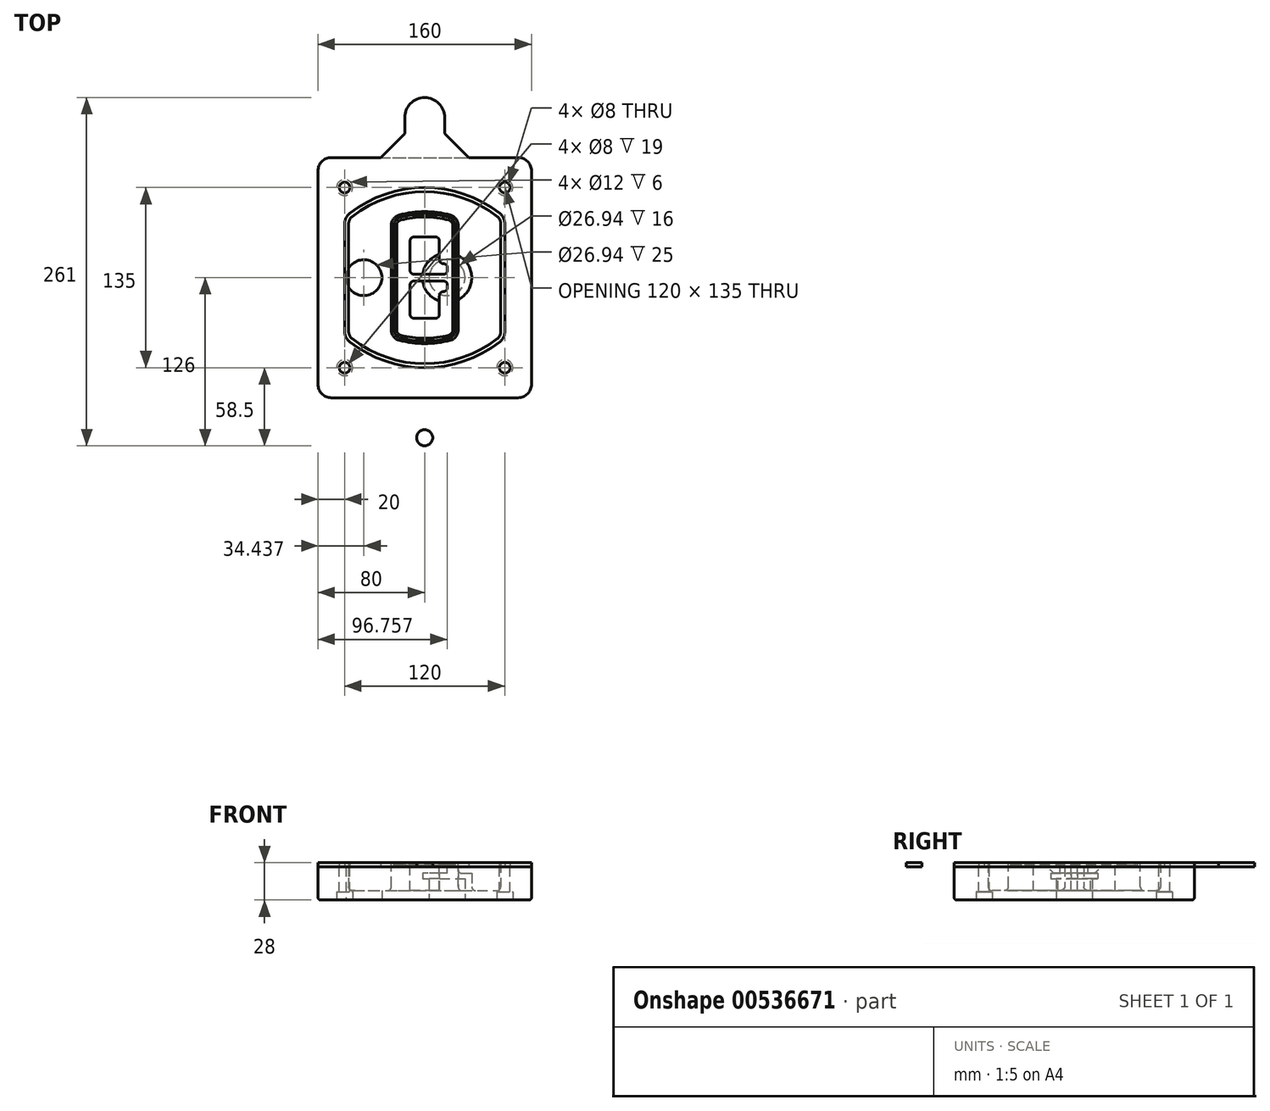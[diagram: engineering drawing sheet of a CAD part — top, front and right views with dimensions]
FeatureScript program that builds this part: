
annotation { "Feature Type Name" : "Feature", "Feature Type Description" : "" }
export const myFeature = defineFeature(function(context is Context, id is Id, definition is map)
    precondition{}
    {
        {
            var Q0;
            Q0=qCreatedBy(makeId("Top.planeOp"),FACE);
            var sketch = newSketch(context, id + "F0", { "sketchPlane" : qUnion([Q0])});
            skPoint(sketch, "E0.rect.middle", {"position": v(0, 0) * mm});
            skLineSegment(sketch, "E1.bottom", {"start": v(-70, -90) * mm, "end": v(70, -90) * mm});
            skLineSegment(sketch, "E1.top", {"start": v(-70, 90) * mm, "end": v(70, 90) * mm});
            skLineSegment(sketch, "E1.left", {"start": v(-80, -80) * mm, "end": v(-80, 80) * mm});
            skLineSegment(sketch, "E1.right", {"start": v(80, -80) * mm, "end": v(80, 80) * mm});
            skLineSegment(sketch, "E2", {"start": v(-80, 90) * mm, "end": v(80, -90) * mm, "construction": true});
            skLineSegment(sketch, "E3", {"start": v(80, 90) * mm, "end": v(-80, -90) * mm, "construction": true});
            skCircle(sketch, "E4", {"center": v(-60, 67.5) * mm, "radius": 4 * mm});
            skCircle(sketch, "E5", {"center": v(60, 67.5) * mm, "radius": 4 * mm});
            skCircle(sketch, "E6", {"center": v(60, -67.5) * mm, "radius": 4 * mm});
            skCircle(sketch, "E7", {"center": v(-60, -67.5) * mm, "radius": 4 * mm});
            skLineSegment(sketch, "E8", {"start": v(-60, 67.5) * mm, "end": v(60, 67.5) * mm, "construction": true});
            skLineSegment(sketch, "E9", {"start": v(60, 67.5) * mm, "end": v(60, -67.5) * mm, "construction": true});
            skLineSegment(sketch, "E10", {"start": v(60, -67.5) * mm, "end": v(-60, -67.5) * mm, "construction": true});
            skLineSegment(sketch, "E11", {"start": v(-60, -67.5) * mm, "end": v(-60, 67.5) * mm, "construction": true});
            skLineSegment(sketch, "E12", {"start": v(-60, 40.3) * mm, "end": v(-60, -40.3) * mm});
            skLineSegment(sketch, "E13", {"start": v(60, 40.3) * mm, "end": v(60, -40.3) * mm});
            skArc(sketch, "E14", {"start": v(56.15, 48.18) * mm, "mid": v(0, 67.5) * mm, "end": v(-56.15, 48.18) * mm});
            skArc(sketch, "E15", {"start": v(-56.15, -48.18) * mm, "mid": v(0, -67.5) * mm, "end": v(56.15, -48.18) * mm});
            skLineSegment(sketch, "E16", {"start": v(-60, 0) * mm, "end": v(60, 0) * mm, "construction": true});
            skPoint(sketch, "E17.visualSharp", {"position": v(-60, -45) * mm});
            skArc(sketch, "E17.filletArc", {"start": v(-60, -40.3) * mm, "mid": v(-58.99, -44.68) * mm, "end": v(-56.15, -48.18) * mm});
            skPoint(sketch, "E18.visualSharp", {"position": v(-60, 45) * mm});
            skArc(sketch, "E18.filletArc", {"start": v(-56.15, 48.18) * mm, "mid": v(-58.99, 44.68) * mm, "end": v(-60, 40.3) * mm});
            skPoint(sketch, "E19.visualSharp", {"position": v(60, 45) * mm});
            skArc(sketch, "E19.filletArc", {"start": v(60, 40.3) * mm, "mid": v(58.99, 44.68) * mm, "end": v(56.15, 48.18) * mm});
            skPoint(sketch, "E20.visualSharp", {"position": v(60, -45) * mm});
            skArc(sketch, "E20.filletArc", {"start": v(56.15, -48.18) * mm, "mid": v(58.99, -44.68) * mm, "end": v(60, -40.3) * mm});
            skPoint(sketch, "E21.visualSharp", {"position": v(-80, 90) * mm});
            skArc(sketch, "E21.filletArc", {"start": v(-70, 90) * mm, "mid": v(-77.07, 87.07) * mm, "end": v(-80, 80) * mm});
            skPoint(sketch, "E22.visualSharp", {"position": v(80, 90) * mm});
            skArc(sketch, "E22.filletArc", {"start": v(80, 80) * mm, "mid": v(77.07, 87.07) * mm, "end": v(70, 90) * mm});
            skPoint(sketch, "E23.visualSharp", {"position": v(80, -90) * mm});
            skArc(sketch, "E23.filletArc", {"start": v(70, -90) * mm, "mid": v(77.07, -87.07) * mm, "end": v(80, -80) * mm});
            skPoint(sketch, "E24.visualSharp", {"position": v(-80, -90) * mm});
            skArc(sketch, "E24.filletArc", {"start": v(-80, -80) * mm, "mid": v(-77.07, -87.07) * mm, "end": v(-70, -90) * mm});
            skArc(sketch, "E25.0", {"start": v(57, 40.3) * mm, "mid": v(56.3, 43.36) * mm, "end": v(54.3, 45.81) * mm});
            skLineSegment(sketch, "E25.1", {"start": v(57, 40.3) * mm, "end": v(57, -40.3) * mm});
            skArc(sketch, "E25.2", {"start": v(54.3, -45.81) * mm, "mid": v(56.3, -43.36) * mm, "end": v(57, -40.3) * mm});
            skArc(sketch, "E25.3", {"start": v(-54.3, -45.81) * mm, "mid": v(0, -64.5) * mm, "end": v(54.3, -45.81) * mm});
            skArc(sketch, "E25.4", {"start": v(-57, -40.3) * mm, "mid": v(-56.3, -43.36) * mm, "end": v(-54.3, -45.81) * mm});
            skArc(sketch, "E25.5", {"start": v(54.3, 45.81) * mm, "mid": v(0, 64.5) * mm, "end": v(-54.3, 45.81) * mm});
            skLineSegment(sketch, "E25.6", {"start": v(-57, 40.3) * mm, "end": v(-57, -40.3) * mm});
            skArc(sketch, "E25.7", {"start": v(-54.3, 45.81) * mm, "mid": v(-56.3, 43.36) * mm, "end": v(-57, 40.3) * mm});
            skArc(sketch, "E26.0", {"start": v(-58.62, 51.33) * mm, "mid": v(-62.58, 46.43) * mm, "end": v(-64, 40.3) * mm});
            skArc(sketch, "E26.1", {"start": v(58.62, 51.33) * mm, "mid": v(0, 71.5) * mm, "end": v(-58.62, 51.33) * mm});
            skArc(sketch, "E26.2", {"start": v(64, 40.3) * mm, "mid": v(62.58, 46.43) * mm, "end": v(58.62, 51.33) * mm});
            skLineSegment(sketch, "E26.3", {"start": v(64, 40.3) * mm, "end": v(64, -40.3) * mm});
            skArc(sketch, "E26.4", {"start": v(58.62, -51.33) * mm, "mid": v(62.58, -46.43) * mm, "end": v(64, -40.3) * mm});
            skLineSegment(sketch, "E26.5", {"start": v(-64, 40.3) * mm, "end": v(-64, -40.3) * mm});
            skArc(sketch, "E26.6", {"start": v(-58.62, -51.33) * mm, "mid": v(0, -71.5) * mm, "end": v(58.62, -51.33) * mm});
            skArc(sketch, "E26.7", {"start": v(-64, -40.3) * mm, "mid": v(-62.58, -46.43) * mm, "end": v(-58.62, -51.33) * mm});
            skSolve(sketch);
        }
        {
            var Q0;
            Q0=makeQuery(id+"F0.imprint","IMPRINT",FACE,{"disambiguationData":[TD([[makeQuery(id+"F0.imprint","IMPRINT",EDGE,{"derivedFrom":sQuery(id+"F0.wireOp",EDGE,"E1.bottom")}),1.0]])]});
            var Q1;
            Q1=makeQuery(id+"F0.imprint","IMPRINT",FACE,{"disambiguationData":[TD([[makeQuery(id+"F0.imprint","IMPRINT",EDGE,{"derivedFrom":sQuery(id+"F0.wireOp",EDGE,"E12")}),1.0]])]});
            var Q2;
            Q2=makeQuery(id+"F0.imprint","IMPRINT",FACE,{"disambiguationData":[TD([[makeQuery(id+"F0.imprint","IMPRINT",EDGE,{"derivedFrom":sQuery(id+"F0.wireOp",EDGE,"E25.0")}),1.0]])]});
            var Q3;
            Q3=makeQuery(id+"F0.imprint","IMPRINT",FACE,{"disambiguationData":[TD([[makeQuery(id+"F0.imprint","IMPRINT",EDGE,{"derivedFrom":sQuery(id+"F0.wireOp",EDGE,"E12")}),-1.0]])]});
            extrude(context, id + "F1", {"entities" : qUnion([Q0, Q1, Q2, Q3]), "oppositeDirection" : true, "depth" : 25 * mm});
        }
        {
            var Q0;
            Q0=makeQuery(id+"F0.imprint","IMPRINT",FACE,{"disambiguationData":[TD([[makeQuery(id+"F0.imprint","IMPRINT",EDGE,{"derivedFrom":sQuery(id+"F0.wireOp",EDGE,"E12")}),1.0]])]});
            extrude(context, id + "F2", {"entities" : qUnion([Q0]), "operationType" : NewBodyOperationType.ADD, "depth" : 3 * mm});
        }
        {
            var Q0;
            Q0=makeQuery(id+"F0.imprint","IMPRINT",FACE,{"disambiguationData":[TD([[makeQuery(id+"F0.imprint","IMPRINT",EDGE,{"derivedFrom":sQuery(id+"F0.wireOp",EDGE,"E25.0")}),1.0]])]});
            extrude(context, id + "F3", {"entities" : qUnion([Q0]), "operationType" : NewBodyOperationType.REMOVE, "oppositeDirection" : true, "depth" : 18 * mm});
        }
        {
            var Q0;
            Q0=makeQuery(id+"F2.opExtrude","CAP_FACE",FACE,{"disambiguationData":[OSD([sQuery(id+"F0.wireOp",EDGE,"E12"),sQuery(id+"F0.wireOp",EDGE,"E13"),sQuery(id+"F0.wireOp",EDGE,"E14"),sQuery(id+"F0.wireOp",EDGE,"E15"),sQuery(id+"F0.wireOp",EDGE,"E17.filletArc"),sQuery(id+"F0.wireOp",EDGE,"E18.filletArc"),sQuery(id+"F0.wireOp",EDGE,"E19.filletArc"),sQuery(id+"F0.wireOp",EDGE,"E20.filletArc"),sQuery(id+"F0.wireOp",EDGE,"E25.0"),sQuery(id+"F0.wireOp",EDGE,"E25.1"),sQuery(id+"F0.wireOp",EDGE,"E25.2"),sQuery(id+"F0.wireOp",EDGE,"E25.3"),sQuery(id+"F0.wireOp",EDGE,"E25.4"),sQuery(id+"F0.wireOp",EDGE,"E25.5"),sQuery(id+"F0.wireOp",EDGE,"E25.6"),sQuery(id+"F0.wireOp",EDGE,"E25.7")])],"isStart":false});
            var sketch = newSketch(context, id + "F4", { "sketchPlane" : qUnion([Q0])});
            skArc(sketch, "E27.0", {"start": v(-19.08, -46.97) * mm, "mid": v(0, -49.5) * mm, "end": v(19.08, -46.97) * mm});
            skArc(sketch, "E28.0", {"start": v(19.08, 46.97) * mm, "mid": v(0, 49.5) * mm, "end": v(-19.08, 46.97) * mm});
            skLineSegment(sketch, "E29", {"start": v(-25, 39.25) * mm, "end": v(-25, -39.25) * mm});
            skLineSegment(sketch, "E30", {"start": v(25, 39.25) * mm, "end": v(25, -39.25) * mm});
            skLineSegment(sketch, "E31", {"start": v(-25, 45.1) * mm, "end": v(25, 45.1) * mm, "construction": true});
            skLineSegment(sketch, "E32", {"start": v(-25, -45.1) * mm, "end": v(25, -45.1) * mm, "construction": true});
            skPoint(sketch, "E33.visualSharp", {"position": v(-25, 45.1) * mm});
            skArc(sketch, "E33.filletArc", {"start": v(-19.08, 46.97) * mm, "mid": v(-23.35, 44.11) * mm, "end": v(-25, 39.25) * mm});
            skPoint(sketch, "E34.visualSharp", {"position": v(25, 45.1) * mm});
            skArc(sketch, "E34.filletArc", {"start": v(25, 39.25) * mm, "mid": v(23.35, 44.11) * mm, "end": v(19.08, 46.97) * mm});
            skPoint(sketch, "E35.visualSharp", {"position": v(25, -45.1) * mm});
            skArc(sketch, "E35.filletArc", {"start": v(19.08, -46.97) * mm, "mid": v(23.35, -44.11) * mm, "end": v(25, -39.25) * mm});
            skPoint(sketch, "E36.visualSharp", {"position": v(-25, -45.1) * mm});
            skArc(sketch, "E36.filletArc", {"start": v(-25, -39.25) * mm, "mid": v(-23.35, -44.11) * mm, "end": v(-19.08, -46.97) * mm});
            skArc(sketch, "E37.0", {"start": v(54.3, 45.81) * mm, "mid": v(0, 64.5) * mm, "end": v(-54.3, 45.81) * mm});
            skArc(sketch, "E37.1", {"start": v(-54.3, 45.81) * mm, "mid": v(-56.3, 43.36) * mm, "end": v(-57, 40.3) * mm});
            skLineSegment(sketch, "E37.2", {"start": v(-57, 40.3) * mm, "end": v(-57, -40.3) * mm});
            skArc(sketch, "E37.3", {"start": v(-57, -40.3) * mm, "mid": v(-56.3, -43.36) * mm, "end": v(-54.3, -45.81) * mm});
            skArc(sketch, "E37.4", {"start": v(-54.3, -45.81) * mm, "mid": v(0, -64.5) * mm, "end": v(54.3, -45.81) * mm});
            skArc(sketch, "E37.5", {"start": v(54.3, -45.81) * mm, "mid": v(56.3, -43.36) * mm, "end": v(57, -40.3) * mm});
            skLineSegment(sketch, "E37.6", {"start": v(57, 40.3) * mm, "end": v(57, -40.3) * mm});
            skArc(sketch, "E37.7", {"start": v(57, 40.3) * mm, "mid": v(56.3, 43.36) * mm, "end": v(54.3, 45.81) * mm});
            skLineSegment(sketch, "E38.0", {"start": v(23, 39.25) * mm, "end": v(23, -39.25) * mm});
            skArc(sketch, "E38.1", {"start": v(18.56, -45.04) * mm, "mid": v(21.76, -42.9) * mm, "end": v(23, -39.25) * mm});
            skArc(sketch, "E38.2", {"start": v(-18.56, -45.04) * mm, "mid": v(0, -47.5) * mm, "end": v(18.56, -45.04) * mm});
            skArc(sketch, "E38.3", {"start": v(-23, -39.25) * mm, "mid": v(-21.76, -42.9) * mm, "end": v(-18.56, -45.04) * mm});
            skLineSegment(sketch, "E38.4", {"start": v(-23, 39.25) * mm, "end": v(-23, -39.25) * mm});
            skArc(sketch, "E38.5", {"start": v(23, 39.25) * mm, "mid": v(21.76, 42.9) * mm, "end": v(18.56, 45.04) * mm});
            skArc(sketch, "E38.6", {"start": v(-18.56, 45.04) * mm, "mid": v(-21.76, 42.9) * mm, "end": v(-23, 39.25) * mm});
            skArc(sketch, "E38.7", {"start": v(18.56, 45.04) * mm, "mid": v(0, 47.5) * mm, "end": v(-18.56, 45.04) * mm});
            skArc(sketch, "E39.0", {"start": v(21, 39.25) * mm, "mid": v(20.18, 41.68) * mm, "end": v(18.04, 43.1) * mm});
            skLineSegment(sketch, "E39.1", {"start": v(21, 39.25) * mm, "end": v(21, -39.25) * mm});
            skArc(sketch, "E39.2", {"start": v(18.04, -43.1) * mm, "mid": v(20.18, -41.68) * mm, "end": v(21, -39.25) * mm});
            skArc(sketch, "E39.3", {"start": v(-18.04, -43.1) * mm, "mid": v(0, -45.5) * mm, "end": v(18.04, -43.1) * mm});
            skArc(sketch, "E39.4", {"start": v(-21, -39.25) * mm, "mid": v(-20.18, -41.68) * mm, "end": v(-18.04, -43.1) * mm});
            skArc(sketch, "E39.5", {"start": v(18.04, 43.1) * mm, "mid": v(0, 45.5) * mm, "end": v(-18.04, 43.1) * mm});
            skLineSegment(sketch, "E39.6", {"start": v(-21, 39.25) * mm, "end": v(-21, -39.25) * mm});
            skArc(sketch, "E39.7", {"start": v(-18.04, 43.1) * mm, "mid": v(-20.18, 41.68) * mm, "end": v(-21, 39.25) * mm});
            skLineSegment(sketch, "E40", {"start": v(-25, 0) * mm, "end": v(25, 0) * mm, "construction": true});
            skLineSegment(sketch, "E41", {"start": v(-11, 5.5) * mm, "end": v(-11, 27.5) * mm});
            skLineSegment(sketch, "E42", {"start": v(-8, 30.5) * mm, "end": v(8, 30.5) * mm});
            skLineSegment(sketch, "E43", {"start": v(11, 27.5) * mm, "end": v(11, 13.5) * mm});
            skLineSegment(sketch, "E44", {"start": v(14, 10.5) * mm, "end": v(14, 10.5) * mm});
            skLineSegment(sketch, "E45", {"start": v(17, 7.5) * mm, "end": v(17, 5.5) * mm});
            skLineSegment(sketch, "E46", {"start": v(14, 2.5) * mm, "end": v(-8, 2.5) * mm});
            skPoint(sketch, "E47.visualSharp", {"position": v(-11, 30.5) * mm});
            skArc(sketch, "E47.filletArc", {"start": v(-8, 30.5) * mm, "mid": v(-10.12, 29.62) * mm, "end": v(-11, 27.5) * mm});
            skPoint(sketch, "E48.visualSharp", {"position": v(11, 30.5) * mm});
            skArc(sketch, "E48.filletArc", {"start": v(11, 27.5) * mm, "mid": v(10.12, 29.62) * mm, "end": v(8, 30.5) * mm});
            skPoint(sketch, "E49.visualSharp", {"position": v(11, 10.5) * mm});
            skArc(sketch, "E49.filletArc", {"start": v(11, 13.5) * mm, "mid": v(11.88, 11.38) * mm, "end": v(14, 10.5) * mm});
            skPoint(sketch, "E50.visualSharp", {"position": v(17, 10.5) * mm});
            skArc(sketch, "E50.filletArc", {"start": v(17, 7.5) * mm, "mid": v(16.12, 9.62) * mm, "end": v(14, 10.5) * mm});
            skPoint(sketch, "E51.visualSharp", {"position": v(17, 2.5) * mm});
            skArc(sketch, "E51.filletArc", {"start": v(14, 2.5) * mm, "mid": v(16.12, 3.38) * mm, "end": v(17, 5.5) * mm});
            skPoint(sketch, "E52.visualSharp", {"position": v(-11, 2.5) * mm});
            skArc(sketch, "E52.filletArc", {"start": v(-11, 5.5) * mm, "mid": v(-10.12, 3.38) * mm, "end": v(-8, 2.5) * mm});
            skLineSegment(sketch, "E53.0.MirrorCS", {"start": v(14, -2.5) * mm, "end": v(-8, -2.5) * mm});
            skArc(sketch, "E54.0.MirrorCS", {"start": v(-11, -5.5) * mm, "mid": v(-10.12, -3.38) * mm, "end": v(-8, -2.5) * mm});
            skLineSegment(sketch, "E55.0.MirrorCS", {"start": v(-11, -5.5) * mm, "end": v(-11, -27.5) * mm});
            skArc(sketch, "E56.0.MirrorCS", {"start": v(-8, -30.5) * mm, "mid": v(-10.12, -29.62) * mm, "end": v(-11, -27.5) * mm});
            skLineSegment(sketch, "E57.0.MirrorCS", {"start": v(-8, -30.5) * mm, "end": v(8, -30.5) * mm});
            skArc(sketch, "E58.0.MirrorCS", {"start": v(11, -27.5) * mm, "mid": v(10.12, -29.62) * mm, "end": v(8, -30.5) * mm});
            skLineSegment(sketch, "E59.0.MirrorCS", {"start": v(11, -27.5) * mm, "end": v(11, -13.5) * mm});
            skArc(sketch, "E60.0.MirrorCS", {"start": v(11, -13.5) * mm, "mid": v(11.88, -11.38) * mm, "end": v(14, -10.5) * mm});
            skArc(sketch, "E61.0.MirrorCS", {"start": v(17, -7.5) * mm, "mid": v(16.12, -9.62) * mm, "end": v(14, -10.5) * mm});
            skLineSegment(sketch, "E62.0.MirrorCS", {"start": v(17, -7.5) * mm, "end": v(17, -5.5) * mm});
            skArc(sketch, "E63.0.MirrorCS", {"start": v(14, -2.5) * mm, "mid": v(16.12, -3.38) * mm, "end": v(17, -5.5) * mm});
            skSolve(sketch);
        }
        {
            var Q0;
            Q0=makeQuery(id+"F4.imprint","IMPRINT",FACE,{"disambiguationData":[TD([[makeQuery(id+"F4.imprint","IMPRINT",EDGE,{"derivedFrom":sQuery(id+"F4.wireOp",EDGE,"E27.0")}),1.0]])]});
            var Q1;
            Q1=makeQuery(id+"F4.imprint","IMPRINT",FACE,{"disambiguationData":[TD([[makeQuery(id+"F4.imprint","IMPRINT",EDGE,{"derivedFrom":sQuery(id+"F4.wireOp",EDGE,"E38.0")}),-1.0]])]});
            var Q2;
            Q2=makeQuery(id+"F4.imprint","IMPRINT",FACE,{"disambiguationData":[TD([[makeQuery(id+"F4.imprint","IMPRINT",EDGE,{"derivedFrom":sQuery(id+"F4.wireOp",EDGE,"E39.0")}),1.0]])]});
            extrude(context, id + "F5", {"entities" : qUnion([Q0, Q1, Q2]), "operationType" : NewBodyOperationType.ADD, "endBound" : BoundingType.UP_TO_NEXT, "oppositeDirection" : true, "depth" : 25 * mm});
        }
        {
            var Q0;
            Q0=makeQuery(id+"F4.imprint","IMPRINT",FACE,{"disambiguationData":[TD([[makeQuery(id+"F4.imprint","IMPRINT",EDGE,{"derivedFrom":sQuery(id+"F4.wireOp",EDGE,"E38.0")}),-1.0]])]});
            extrude(context, id + "F6", {"entities" : qUnion([Q0]), "operationType" : NewBodyOperationType.REMOVE, "oppositeDirection" : true, "depth" : 2 * mm});
        }
        {
            var Q0;
            Q0=makeQuery(id+"F1.opExtrude","CAP_FACE",FACE,{"disambiguationData":[OSD([sQuery(id+"F0.wireOp",EDGE,"E1.bottom"),sQuery(id+"F0.wireOp",EDGE,"E1.top"),sQuery(id+"F0.wireOp",EDGE,"E1.left"),sQuery(id+"F0.wireOp",EDGE,"E1.right"),sQuery(id+"F0.wireOp",EDGE,"E4"),sQuery(id+"F0.wireOp",EDGE,"E5"),sQuery(id+"F0.wireOp",EDGE,"E6"),sQuery(id+"F0.wireOp",EDGE,"E7"),sQuery(id+"F0.wireOp",EDGE,"E21.filletArc"),sQuery(id+"F0.wireOp",EDGE,"E22.filletArc"),sQuery(id+"F0.wireOp",EDGE,"E23.filletArc"),sQuery(id+"F0.wireOp",EDGE,"E24.filletArc")])],"isStart":false});
            var sketch = newSketch(context, id + "F7", { "sketchPlane" : qUnion([Q0])});
            skCircle(sketch, "E64", {"center": v(16.76, 0) * mm, "radius": 13.47 * mm});
            skCircle(sketch, "E65", {"center": v(-45.56, 0) * mm, "radius": 13.47 * mm});
            skLineSegment(sketch, "E66", {"start": v(80, 0) * mm, "end": v(-80, 0) * mm});
            skCircle(sketch, "E67", {"center": v(16.76, 0) * mm, "radius": 18.47 * mm});
            skCircle(sketch, "E68", {"center": v(60, -67.5) * mm, "radius": 6 * mm});
            skCircle(sketch, "E69", {"center": v(-60, -67.5) * mm, "radius": 6 * mm});
            skCircle(sketch, "E70", {"center": v(-60, 67.5) * mm, "radius": 6 * mm});
            skCircle(sketch, "E71", {"center": v(60, 67.5) * mm, "radius": 6 * mm});
            skSolve(sketch);
        }
        {
            var Q0;
            {var subQ1=sQuery(id+"F7.wireOp",EDGE,"E66");var subQ4=sQuery(id+"F7.wireOp",EDGE,"E64");var subQ6=makeQuery(id+"F7.imprint","INTERSECT",VERTEX,{"disambiguationData":[OD(0.0)],"derivedFrom":[subQ4,subQ1]});Q0=makeQuery(id+"F7.imprint","IMPRINT",FACE,{"disambiguationData":[TD([[makeQuery(id+"F7.imprint","IMPRINT",EDGE,{"disambiguationData":[TD([[subQ6,-1.0]])],"derivedFrom":subQ4}),-1.0]])]});}
            var Q1;
            {var subQ0=sQuery(id+"F7.wireOp",EDGE,"E66");var subQ1=sQuery(id+"F7.wireOp",EDGE,"E64");var subQ3=makeQuery(id+"F7.imprint","INTERSECT",VERTEX,{"disambiguationData":[OD(0.0)],"derivedFrom":[subQ1,subQ0]});Q1=makeQuery(id+"F7.imprint","IMPRINT",FACE,{"disambiguationData":[TD([[makeQuery(id+"F7.imprint","IMPRINT",EDGE,{"disambiguationData":[TD([[subQ3,-1.0]])],"derivedFrom":subQ1}),1.0]])]});}
            var Q2;
            {var subQ0=sQuery(id+"F7.wireOp",EDGE,"E66");var subQ1=sQuery(id+"F7.wireOp",EDGE,"E64");var subQ3=makeQuery(id+"F7.imprint","INTERSECT",VERTEX,{"disambiguationData":[OD(0.0)],"derivedFrom":[subQ1,subQ0]});Q2=makeQuery(id+"F7.imprint","IMPRINT",FACE,{"disambiguationData":[TD([[makeQuery(id+"F7.imprint","IMPRINT",EDGE,{"disambiguationData":[TD([[subQ3,1.0]])],"derivedFrom":subQ1}),1.0]])]});}
            var Q3;
            {var subQ1=sQuery(id+"F7.wireOp",EDGE,"E66");var subQ4=sQuery(id+"F7.wireOp",EDGE,"E64");var subQ6=makeQuery(id+"F7.imprint","INTERSECT",VERTEX,{"disambiguationData":[OD(0.0)],"derivedFrom":[subQ4,subQ1]});Q3=makeQuery(id+"F7.imprint","IMPRINT",FACE,{"disambiguationData":[TD([[makeQuery(id+"F7.imprint","IMPRINT",EDGE,{"disambiguationData":[TD([[subQ6,1.0]])],"derivedFrom":subQ4}),-1.0]])]});}
            extrude(context, id + "F8", {"entities" : qUnion([Q0, Q1, Q2, Q3]), "operationType" : NewBodyOperationType.ADD, "oppositeDirection" : true, "depth" : 20 * mm});
        }
        {
            var Q0;
            {var subQ0=sQuery(id+"F7.wireOp",EDGE,"E66");var subQ1=sQuery(id+"F7.wireOp",EDGE,"E64");var subQ3=makeQuery(id+"F7.imprint","INTERSECT",VERTEX,{"disambiguationData":[OD(0.0)],"derivedFrom":[subQ1,subQ0]});Q0=makeQuery(id+"F7.imprint","IMPRINT",FACE,{"disambiguationData":[TD([[makeQuery(id+"F7.imprint","IMPRINT",EDGE,{"disambiguationData":[TD([[subQ3,-1.0]])],"derivedFrom":subQ1}),1.0]])]});}
            var Q1;
            {var subQ0=sQuery(id+"F7.wireOp",EDGE,"E66");var subQ1=sQuery(id+"F7.wireOp",EDGE,"E64");var subQ3=makeQuery(id+"F7.imprint","INTERSECT",VERTEX,{"disambiguationData":[OD(0.0)],"derivedFrom":[subQ1,subQ0]});Q1=makeQuery(id+"F7.imprint","IMPRINT",FACE,{"disambiguationData":[TD([[makeQuery(id+"F7.imprint","IMPRINT",EDGE,{"disambiguationData":[TD([[subQ3,1.0]])],"derivedFrom":subQ1}),1.0]])]});}
            extrude(context, id + "F9", {"entities" : qUnion([Q0, Q1]), "operationType" : NewBodyOperationType.REMOVE, "oppositeDirection" : true, "depth" : 16 * mm});
        }
        {
            var Q0;
            {var subQ0=sQuery(id+"F7.wireOp",EDGE,"E66");var subQ1=sQuery(id+"F7.wireOp",EDGE,"E65");var subQ3=makeQuery(id+"F7.imprint","INTERSECT",VERTEX,{"disambiguationData":[OD(0.0)],"derivedFrom":[subQ1,subQ0]});Q0=makeQuery(id+"F7.imprint","IMPRINT",FACE,{"disambiguationData":[TD([[makeQuery(id+"F7.imprint","IMPRINT",EDGE,{"disambiguationData":[TD([[subQ3,-1.0]])],"derivedFrom":subQ1}),1.0]])]});}
            var Q1;
            {var subQ0=sQuery(id+"F7.wireOp",EDGE,"E66");var subQ1=sQuery(id+"F7.wireOp",EDGE,"E65");var subQ3=makeQuery(id+"F7.imprint","INTERSECT",VERTEX,{"disambiguationData":[OD(0.0)],"derivedFrom":[subQ1,subQ0]});Q1=makeQuery(id+"F7.imprint","IMPRINT",FACE,{"disambiguationData":[TD([[makeQuery(id+"F7.imprint","IMPRINT",EDGE,{"disambiguationData":[TD([[subQ3,1.0]])],"derivedFrom":subQ1}),1.0]])]});}
            extrude(context, id + "F10", {"entities" : qUnion([Q0, Q1]), "operationType" : NewBodyOperationType.REMOVE, "oppositeDirection" : true, "depth" : 25 * mm});
        }
        {
            var Q0;
            Q0=makeQuery(id+"F7.imprint","IMPRINT",FACE,{"disambiguationData":[TD([[makeQuery(id+"F7.imprint","IMPRINT",EDGE,{"derivedFrom":sQuery(id+"F7.wireOp",EDGE,"E68")}),1.0]])]});
            var Q1;
            Q1=makeQuery(id+"F7.imprint","IMPRINT",FACE,{"disambiguationData":[TD([[makeQuery(id+"F7.imprint","IMPRINT",EDGE,{"derivedFrom":makeQuery(id+"F1.opExtrude","CAP_EDGE",EDGE,{"disambiguationData":[OSD([sQuery(id+"F0.wireOp",EDGE,"E5")])],"isStart":false})}),-1.0]])]});
            var Q2;
            Q2=makeQuery(id+"F7.imprint","IMPRINT",FACE,{"disambiguationData":[TD([[makeQuery(id+"F7.imprint","IMPRINT",EDGE,{"derivedFrom":sQuery(id+"F7.wireOp",EDGE,"E69")}),1.0]])]});
            var Q3;
            Q3=makeQuery(id+"F7.imprint","IMPRINT",FACE,{"disambiguationData":[TD([[makeQuery(id+"F7.imprint","IMPRINT",EDGE,{"derivedFrom":makeQuery(id+"F1.opExtrude","CAP_EDGE",EDGE,{"disambiguationData":[OSD([sQuery(id+"F0.wireOp",EDGE,"E4")])],"isStart":false})}),-1.0]])]});
            var Q4;
            Q4=makeQuery(id+"F7.imprint","IMPRINT",FACE,{"disambiguationData":[TD([[makeQuery(id+"F7.imprint","IMPRINT",EDGE,{"derivedFrom":sQuery(id+"F7.wireOp",EDGE,"E70")}),1.0]])]});
            var Q5;
            Q5=makeQuery(id+"F7.imprint","IMPRINT",FACE,{"disambiguationData":[TD([[makeQuery(id+"F7.imprint","IMPRINT",EDGE,{"derivedFrom":makeQuery(id+"F1.opExtrude","CAP_EDGE",EDGE,{"disambiguationData":[OSD([sQuery(id+"F0.wireOp",EDGE,"E7")])],"isStart":false})}),-1.0]])]});
            var Q6;
            Q6=makeQuery(id+"F7.imprint","IMPRINT",FACE,{"disambiguationData":[TD([[makeQuery(id+"F7.imprint","IMPRINT",EDGE,{"derivedFrom":sQuery(id+"F7.wireOp",EDGE,"E71")}),1.0]])]});
            var Q7;
            Q7=makeQuery(id+"F7.imprint","IMPRINT",FACE,{"disambiguationData":[TD([[makeQuery(id+"F7.imprint","IMPRINT",EDGE,{"derivedFrom":makeQuery(id+"F1.opExtrude","CAP_EDGE",EDGE,{"disambiguationData":[OSD([sQuery(id+"F0.wireOp",EDGE,"E6")])],"isStart":false})}),-1.0]])]});
            extrude(context, id + "F11", {"entities" : qUnion([Q0, Q1, Q2, Q3, Q4, Q5, Q6, Q7]), "operationType" : NewBodyOperationType.REMOVE, "oppositeDirection" : true, "depth" : 6 * mm});
        }
        {
            var Q0;
            Q0=makeQuery(id+"F9.boolean.opBoolean","COPY",FACE,{"derivedFrom":makeQuery(id+"F9.opExtrude","CAP_FACE",FACE,{"disambiguationData":[OSD([sQuery(id+"F7.wireOp",EDGE,"E64")])],"isStart":false})});
            var sketch = newSketch(context, id + "F12", { "sketchPlane" : qUnion([Q0])});
            skArc(sketch, "E72.0", {"start": v(11, 17.55) * mm, "mid": v(2.57, 11.82) * mm, "end": v(-1.54, 2.5) * mm});
            skArc(sketch, "E72.1", {"start": v(-1.54, -2.5) * mm, "mid": v(2.57, -11.82) * mm, "end": v(11, -17.55) * mm});
            skLineSegment(sketch, "E73", {"start": v(-1.54, -2.5) * mm, "end": v(14, -2.5) * mm});
            skLineSegment(sketch, "E74.0", {"start": v(14, 2.5) * mm, "end": v(-1.54, 2.5) * mm});
            skArc(sketch, "E74.1", {"start": v(14, 2.5) * mm, "mid": v(16.12, 3.38) * mm, "end": v(17, 5.5) * mm});
            skLineSegment(sketch, "E74.2", {"start": v(17, 7.5) * mm, "end": v(17, 5.5) * mm});
            skArc(sketch, "E74.3", {"start": v(17, 7.5) * mm, "mid": v(16.12, 9.62) * mm, "end": v(14, 10.5) * mm});
            skArc(sketch, "E74.4", {"start": v(11, 13.5) * mm, "mid": v(11.88, 11.38) * mm, "end": v(14, 10.5) * mm});
            skLineSegment(sketch, "E74.5", {"start": v(11, 17.55) * mm, "end": v(11, 13.5) * mm});
            skLineSegment(sketch, "E74.7", {"start": v(14, -2.5) * mm, "end": v(-1.54, -2.5) * mm});
            skArc(sketch, "E74.8", {"start": v(14, -2.5) * mm, "mid": v(16.12, -3.38) * mm, "end": v(17, -5.5) * mm});
            skLineSegment(sketch, "E74.9", {"start": v(17, -7.5) * mm, "end": v(17, -5.5) * mm});
            skArc(sketch, "E74.10", {"start": v(17, -7.5) * mm, "mid": v(16.12, -9.62) * mm, "end": v(14, -10.5) * mm});
            skArc(sketch, "E74.11", {"start": v(11, -13.5) * mm, "mid": v(11.88, -11.38) * mm, "end": v(14, -10.5) * mm});
            skLineSegment(sketch, "E74.12", {"start": v(11, -17.55) * mm, "end": v(11, -13.5) * mm});
            skPoint(sketch, "E75.orphan", {"position": v(11, -27.5) * mm});
            skPoint(sketch, "E76.orphan", {"position": v(-8, -2.5) * mm});
            skPoint(sketch, "E77.orphan", {"position": v(-8, 2.5) * mm});
            skPoint(sketch, "E78.orphan", {"position": v(11, 27.5) * mm});
            skSolve(sketch);
        }
        {
            var Q0;
            {var subQ7=sQuery(id+"F12.wireOp",EDGE,"E72.0");var subQ14=sQuery(id+"F12.wireOp",EDGE,"E72.1");var subQ16=sQuery(id+"F12.wireOp",EDGE,"E74.1");var subQ18=sQuery(id+"F12.wireOp",EDGE,"E74.8");Q0=qUnion([makeQuery(id+"F12.imprint","IMPRINT",FACE,{"disambiguationData":[TD([[makeQuery(id+"F12.imprint","IMPRINT",EDGE,{"derivedFrom":subQ7}),1.0]])]}),makeQuery(id+"F12.imprint","IMPRINT",FACE,{"disambiguationData":[TD([[makeQuery(id+"F12.imprint","IMPRINT",EDGE,{"derivedFrom":subQ14}),1.0]])]}),makeQuery(id+"F12.imprint","IMPRINT",FACE,{"disambiguationData":[TD([[makeQuery(id+"F12.imprint","IMPRINT",EDGE,{"derivedFrom":subQ16}),1.0]])]}),makeQuery(id+"F12.imprint","IMPRINT",FACE,{"disambiguationData":[TD([[makeQuery(id+"F12.imprint","IMPRINT",EDGE,{"derivedFrom":subQ18}),-1.0]])]})]);}
            var Q1;
            Q1=makeQuery(id+"F5.boolean.opBoolean","SPLIT",FACE,{"disambiguationData":[TD([makeQuery(id+"F5.opExtrude","SWEPT_FACE",FACE,{"disambiguationData":[OSD([sQuery(id+"F4.wireOp",EDGE,"E41")])]})])],"derivedFrom":makeQuery(id+"F3.boolean.opBoolean","COPY",FACE,{"derivedFrom":makeQuery(id+"F3.opExtrude","CAP_FACE",FACE,{"disambiguationData":[OSD([sQuery(id+"F0.wireOp",EDGE,"E25.0"),sQuery(id+"F0.wireOp",EDGE,"E25.1"),sQuery(id+"F0.wireOp",EDGE,"E25.2"),sQuery(id+"F0.wireOp",EDGE,"E25.3"),sQuery(id+"F0.wireOp",EDGE,"E25.4"),sQuery(id+"F0.wireOp",EDGE,"E25.5"),sQuery(id+"F0.wireOp",EDGE,"E25.6"),sQuery(id+"F0.wireOp",EDGE,"E25.7")])],"isStart":false})})});
            extrude(context, id + "F13", {"entities" : qUnion([Q0]), "operationType" : NewBodyOperationType.REMOVE, "endBound" : BoundingType.UP_TO_SURFACE, "endBoundEntityFace" : qUnion([Q1]), "depth" : 25 * mm});
        }
        {
            var Q0;
            Q0=makeQuery(id+"F3.boolean.opBoolean","COPY",EDGE,{"derivedFrom":makeQuery(id+"F3.opExtrude","CAP_EDGE",EDGE,{"disambiguationData":[OSD([sQuery(id+"F0.wireOp",EDGE,"E25.6")])],"isStart":false})});
            var Q1;
            Q1=makeQuery(id+"F8.boolean.opBoolean","INTERSECT",EDGE,{"derivedFrom":[makeQuery(id+"F5.opExtrude","SWEPT_FACE",FACE,{"disambiguationData":[OSD([sQuery(id+"F4.wireOp",EDGE,"E30")])]}),makeQuery(id+"F8.opExtrude","CAP_FACE",FACE,{"disambiguationData":[OSD([sQuery(id+"F7.wireOp",EDGE,"E67")])],"isStart":false})]});
            var Q2;
            Q2=makeQuery(id+"F8.boolean.opBoolean","INTERSECT",EDGE,{"disambiguationData":[OD(1.0)],"derivedFrom":[makeQuery(id+"F5.opExtrude","SWEPT_FACE",FACE,{"disambiguationData":[OSD([sQuery(id+"F4.wireOp",EDGE,"E30")])]}),makeQuery(id+"F8.opExtrude","SWEPT_FACE",FACE,{"disambiguationData":[OSD([sQuery(id+"F7.wireOp",EDGE,"E67")])]})]});
            var Q3;
            {var subQ0=sQuery(id+"F4.wireOp",EDGE,"E30");Q3=makeQuery(id+"F8.boolean.opBoolean","SPLIT",EDGE,{"disambiguationData":[TD([makeQuery(id+"F5.opExtrude","SWEPT_FACE",FACE,{"disambiguationData":[OSD([sQuery(id+"F4.wireOp",EDGE,"E35.filletArc")])]})])],"derivedFrom":makeQuery(id+"F5.opExtrude","CAP_EDGE",EDGE,{"disambiguationData":[OSD([subQ0])],"isStart":false})});}
            var Q4;
            {var subQ0=sQuery(id+"F0.wireOp",EDGE,"E25.7");var subQ1=sQuery(id+"F0.wireOp",EDGE,"E25.1");var subQ2=sQuery(id+"F0.wireOp",EDGE,"E25.6");var subQ3=sQuery(id+"F0.wireOp",EDGE,"E25.5");var subQ4=sQuery(id+"F0.wireOp",EDGE,"E25.4");var subQ5=sQuery(id+"F0.wireOp",EDGE,"E25.0");var subQ6=sQuery(id+"F0.wireOp",EDGE,"E25.2");var subQ7=sQuery(id+"F0.wireOp",EDGE,"E25.3");Q4=makeQuery(id+"F8.boolean.opBoolean","INTERSECT",EDGE,{"derivedFrom":[makeQuery(id+"F5.boolean.opBoolean","SPLIT",FACE,{"disambiguationData":[TD([makeQuery(id+"F2.opExtrude","SWEPT_FACE",FACE,{"disambiguationData":[OSD([subQ5])]})])],"derivedFrom":makeQuery(id+"F3.boolean.opBoolean","COPY",FACE,{"derivedFrom":makeQuery(id+"F3.opExtrude","CAP_FACE",FACE,{"disambiguationData":[OSD([subQ5,subQ1,subQ6,subQ7,subQ4,subQ3,subQ2,subQ0])],"isStart":false})})}),makeQuery(id+"F8.opExtrude","SWEPT_FACE",FACE,{"disambiguationData":[OSD([sQuery(id+"F7.wireOp",EDGE,"E67")])]})]});}
            var Q5;
            Q5=makeQuery(id+"F8.boolean.opBoolean","INTERSECT",EDGE,{"disambiguationData":[OD(0.0)],"derivedFrom":[makeQuery(id+"F5.opExtrude","SWEPT_FACE",FACE,{"disambiguationData":[OSD([sQuery(id+"F4.wireOp",EDGE,"E30")])]}),makeQuery(id+"F8.opExtrude","SWEPT_FACE",FACE,{"disambiguationData":[OSD([sQuery(id+"F7.wireOp",EDGE,"E67")])]})]});
            fillet(context, id + "F14", {"entities" : qUnion([Q0, Q1, Q2, Q3, Q4, Q5]), "radius" : 3 * mm, "tangentPropagation" : true, "allowEdgeOverflow" : false});
        }
        {
            var Q0;
            Q0=makeQuery(id+"F1.opExtrude","CAP_EDGE",EDGE,{"disambiguationData":[OSD([sQuery(id+"F0.wireOp",EDGE,"E1.bottom")])],"isStart":false});
            fillet(context, id + "F15", {"entities" : qUnion([Q0]), "radius" : 2 * mm, "tangentPropagation" : true, "allowEdgeOverflow" : false});
        }
        {
            var Q0;
            {var subQ0=sQuery(id+"F0.wireOp",EDGE,"E21.filletArc");var subQ1=sQuery(id+"F0.wireOp",EDGE,"E7");var subQ2=sQuery(id+"F0.wireOp",EDGE,"E6");var subQ3=sQuery(id+"F0.wireOp",EDGE,"E5");var subQ4=sQuery(id+"F0.wireOp",EDGE,"E4");var subQ5=sQuery(id+"F0.wireOp",EDGE,"E22.filletArc");var subQ6=sQuery(id+"F0.wireOp",EDGE,"E1.bottom");var subQ7=sQuery(id+"F0.wireOp",EDGE,"E1.right");var subQ8=sQuery(id+"F0.wireOp",EDGE,"E1.top");var subQ9=sQuery(id+"F0.wireOp",EDGE,"E1.left");var subQ10=sQuery(id+"F0.wireOp",EDGE,"E23.filletArc");var subQ11=sQuery(id+"F0.wireOp",EDGE,"E24.filletArc");Q0=makeQuery(id+"F2.boolean.opBoolean","SPLIT",FACE,{"disambiguationData":[TD([makeQuery(id+"F1.opExtrude","SWEPT_FACE",FACE,{"disambiguationData":[OSD([subQ6])]})])],"derivedFrom":makeQuery(id+"F1.opExtrude","CAP_FACE",FACE,{"disambiguationData":[OSD([subQ6,subQ8,subQ9,subQ7,subQ4,subQ3,subQ2,subQ1,subQ0,subQ5,subQ10,subQ11])],"isStart":true})});}
            var sketch = newSketch(context, id + "F16", { "sketchPlane" : qUnion([Q0])});
            skLineSegment(sketch, "E79", {"start": v(0, 90) * mm, "end": v(0, 120) * mm, "construction": true});
            skCircle(sketch, "E80", {"center": v(0, 120) * mm, "radius": 6 * mm});
            skArc(sketch, "E81", {"start": v(-15, 120) * mm, "mid": v(0, 135) * mm, "end": v(15, 120) * mm});
            skLineSegment(sketch, "E82", {"start": v(-15, 120) * mm, "end": v(-15, 108) * mm});
            skLineSegment(sketch, "E83", {"start": v(-15, 108) * mm, "end": v(-33, 90) * mm});
            skLineSegment(sketch, "E84", {"start": v(15, 120) * mm, "end": v(15, 108) * mm});
            skLineSegment(sketch, "E85", {"start": v(15, 108) * mm, "end": v(33, 90) * mm});
            skLineSegment(sketch, "E86", {"start": v(-15, 108) * mm, "end": v(-15, 90) * mm, "construction": true});
            skLineSegment(sketch, "E87", {"start": v(15, 108) * mm, "end": v(15, 90) * mm, "construction": true});
            skLineSegment(sketch, "E88", {"start": v(-33, 90) * mm, "end": v(-15, 90) * mm, "construction": true});
            skLineSegment(sketch, "E89", {"start": v(15, 90) * mm, "end": v(33, 90) * mm, "construction": true});
            skLineSegment(sketch, "E90", {"start": v(-80, 0) * mm, "end": v(80, 0) * mm, "construction": true});
            skLineSegment(sketch, "E91.MirrorCS", {"start": v(15, -90) * mm, "end": v(33, -90) * mm, "construction": true});
            skLineSegment(sketch, "E92.MirrorCS", {"start": v(-33, -90) * mm, "end": v(-15, -90) * mm, "construction": true});
            skLineSegment(sketch, "E93.MirrorCS", {"start": v(15, -108) * mm, "end": v(15, -90) * mm, "construction": true});
            skCircle(sketch, "E94.MirrorC", {"center": v(0, -120) * mm, "radius": 6 * mm});
            skLineSegment(sketch, "E95.MirrorCS", {"start": v(0, -90) * mm, "end": v(0, -120) * mm, "construction": true});
            skLineSegment(sketch, "E96.MirrorCS", {"start": v(15, -108) * mm, "end": v(33, -90) * mm});
            skLineSegment(sketch, "E97.MirrorCS", {"start": v(-15, -108) * mm, "end": v(-33, -90) * mm});
            skLineSegment(sketch, "E98.MirrorCS", {"start": v(-15, -108) * mm, "end": v(-15, -90) * mm, "construction": true});
            skLineSegment(sketch, "E99.MirrorCS", {"start": v(-15, -120) * mm, "end": v(-15, -108) * mm});
            skArc(sketch, "E100.MirrorCS", {"start": v(-15, -120) * mm, "mid": v(0, -135) * mm, "end": v(15, -120) * mm});
            skLineSegment(sketch, "E101.MirrorCS", {"start": v(15, -120) * mm, "end": v(15, -108) * mm});
            skSolve(sketch);
        }
        {
            var Q0;
            Q0 = qSketchRegion(id + "F16", true);
            var Q1;
            Q1=makeQuery(id+"F16.imprint","IMPRINT",FACE,{"disambiguationData":[TD([[makeQuery(id+"F16.imprint","IMPRINT",EDGE,{"derivedFrom":makeQuery(id+"F1.opExtrude","CAP_EDGE",EDGE,{"disambiguationData":[OSD([sQuery(id+"F0.wireOp",EDGE,"E1.left")])],"isStart":true})}),-1.0]])]});
            var Q2;
            Q2=makeQuery(id+"F16.imprint","IMPRINT",FACE,{"disambiguationData":[TD([[makeQuery(id+"F16.imprint","IMPRINT",EDGE,{"derivedFrom":sQuery(id+"F16.wireOp",EDGE,"E94.MirrorC")}),1.0]])]});
            var Q3;
            Q3=makeQuery(id+"F16.imprint","IMPRINT",FACE,{"disambiguationData":[TD([[makeQuery(id+"F16.imprint","IMPRINT",EDGE,{"derivedFrom":sQuery(id+"F16.wireOp",EDGE,"E80")}),-1.0]])]});
            var Q4;
            Q4=makeQuery(id+"F2.opExtrude","CAP_FACE",FACE,{"disambiguationData":[OSD([sQuery(id+"F0.wireOp",EDGE,"E12"),sQuery(id+"F0.wireOp",EDGE,"E13"),sQuery(id+"F0.wireOp",EDGE,"E14"),sQuery(id+"F0.wireOp",EDGE,"E15"),sQuery(id+"F0.wireOp",EDGE,"E17.filletArc"),sQuery(id+"F0.wireOp",EDGE,"E18.filletArc"),sQuery(id+"F0.wireOp",EDGE,"E19.filletArc"),sQuery(id+"F0.wireOp",EDGE,"E20.filletArc"),sQuery(id+"F0.wireOp",EDGE,"E25.0"),sQuery(id+"F0.wireOp",EDGE,"E25.1"),sQuery(id+"F0.wireOp",EDGE,"E25.2"),sQuery(id+"F0.wireOp",EDGE,"E25.3"),sQuery(id+"F0.wireOp",EDGE,"E25.4"),sQuery(id+"F0.wireOp",EDGE,"E25.5"),sQuery(id+"F0.wireOp",EDGE,"E25.6"),sQuery(id+"F0.wireOp",EDGE,"E25.7")])],"isStart":false});
            extrude(context, id + "F17", {"entities" : qUnion([Q0, Q1, Q2, Q3]), "endBound" : BoundingType.UP_TO_SURFACE, "depth" : 25 * mm, "endBoundEntityFace" : qUnion([Q4]), "offsetDistance" : 25 * mm});
        }
    });
